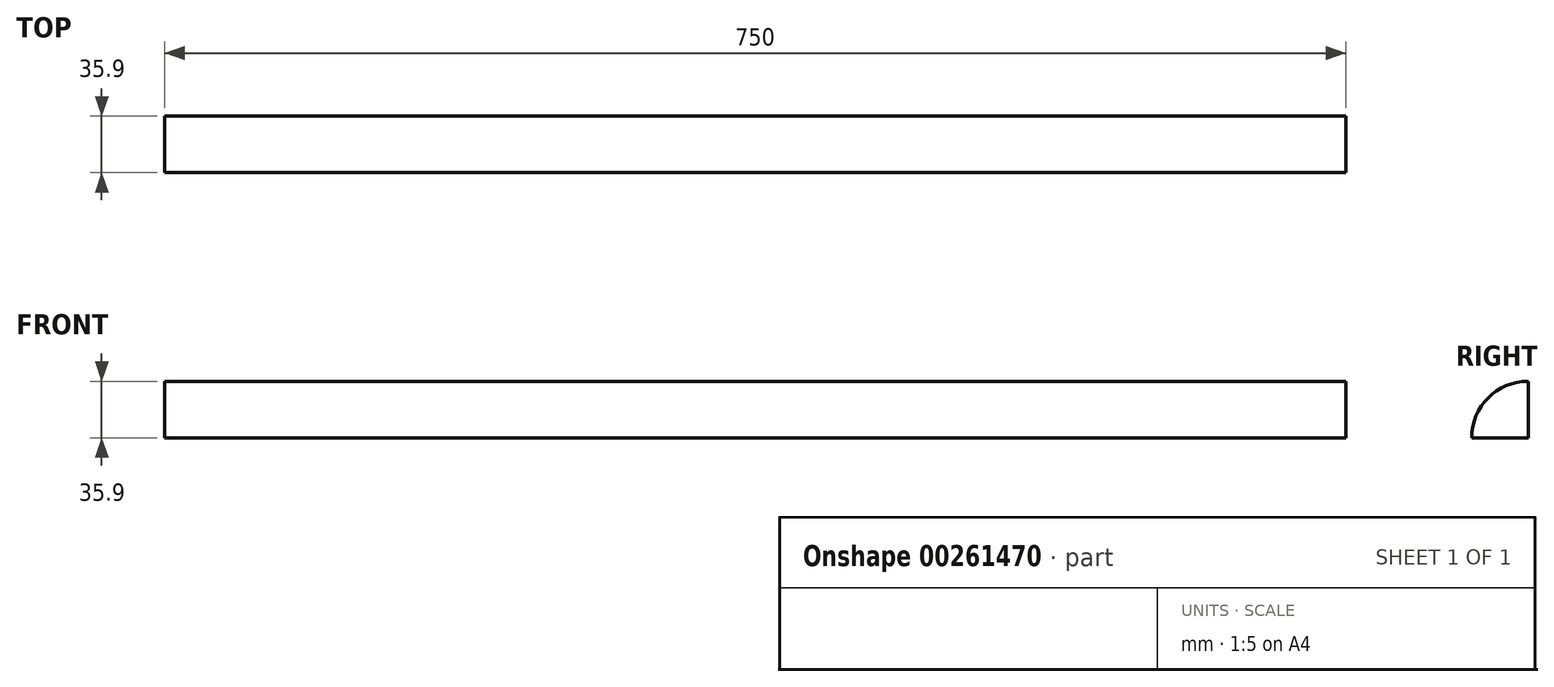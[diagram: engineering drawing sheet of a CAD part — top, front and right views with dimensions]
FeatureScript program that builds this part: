
annotation { "Feature Type Name" : "Feature", "Feature Type Description" : "" }
export const myFeature = defineFeature(function(context is Context, id is Id, definition is map)
    precondition{}
    {
        {
            var Q0;
            Q0=qCreatedBy(makeId("Front.planeOp"),FACE);
            var sketch = newSketch(context, id + "F0", { "sketchPlane" : qUnion([Q0])});
            skLineSegment(sketch, "E0.bottom", {"start": v(0, 35.9) * mm, "end": v(750, 35.9) * mm});
            skLineSegment(sketch, "E0.top", {"start": v(0, 0) * mm, "end": v(750, 0) * mm});
            skLineSegment(sketch, "E0.left", {"start": v(0, 35.9) * mm, "end": v(0, 0) * mm});
            skLineSegment(sketch, "E0.right", {"start": v(750, 35.9) * mm, "end": v(750, 0) * mm});
            skLineSegment(sketch, "E1.bottom", {"start": v(0, 24.08) * mm, "end": v(0, 24.08) * mm});
            skLineSegment(sketch, "E1.top", {"start": v(0, 35.9) * mm, "end": v(0, 35.9) * mm});
            skLineSegment(sketch, "E1.left", {"start": v(0, 35.9) * mm, "end": v(0, 24.08) * mm});
            skLineSegment(sketch, "E1.right", {"start": v(0, 35.9) * mm, "end": v(0, 24.08) * mm});
            skSolve(sketch);
        }
        {
            var Q0;
            Q0=makeQuery(id+"F0.imprint","IMPRINT",FACE,{"disambiguationData":[TD([[makeQuery(id+"F0.imprint","IMPRINT",EDGE,{"derivedFrom":sQuery(id+"F0.wireOp",EDGE,"E0.bottom")}),-1.0]])]});
            var Q1;
            Q1=sQuery(id+"F0.wireOp",EDGE,"E0.bottom");
            var Q2;
            Q2=sQuery(id+"F0.wireOp",EDGE,"E0.top");
            var Q3;
            Q3=sQuery(id+"F0.wireOp",EDGE,"E0.top");
            revolve(context, id + "F1", {"entities" : qUnion([Q0]), "surfaceEntities" : qUnion([Q1, Q2]), "axis" : qUnion([Q3]), "revolveType" : RevolveType.ONE_DIRECTION, "angle" : 90 * degree});
        }
    });
